# Revit family: PRD_AR_WCSqtngPns_CampusSquatPan_CMPX504
name_source: partatom
category: Plumbing Fixtures
revit_build: Autodesk Revit 2018 (Build: 20190510_1515(x64)
units: mm (PartAtom-declared; Revit-internal decimal feet)

## family parameters
Always vertical = Yes
Cut with Voids When Loaded = Yes
OmniClass Number = 23.45.05.21.11.11
OmniClass Title = Water Operated Water Closets
Part Type = Normal
Room Calculation Point = No
Round Connector Dimension = Use Diameter
Shared = No
Work Plane-Based = No

## types (1)
- CMPX504
    AssetType = Fixed
    BIMObjectName = PRD_AR_WCSquattingPans_CampusSquatPan_CMPX504
    Category = Pr_40_20_93_96, WC squatting pans
    Color = Chrome
    Description = Squat pan made of stainless steel, suitable for DN 20 in-wall flush valves, surface satin finished, material thickness 1 mm, 9 liter flushing capacity, with circular folded edge (22 mm) and circular flushing rim. Vertical connection from behind with screw connection of 28 mm diameter, internal DN 100 waste outlet, fixing material and height adjustment included.
    DurationUnit = year
    Features = stainless steel, 1.00 mm, satin finished, inset floor mounting, 755x185x755 mm (WxHxD)
    Finish = Satin finished
    Form = Squatting, washdown
    GrossWeight = 16.00 kg
    IfcExportAs = IfcSanitaryTerminalType
    IfcExportType = TOILETPAN
    IntegralAccessories = Internal DN 100 waste outlet, fixing material and height adjustment included.
    Manufacturer = KWC Group AG
    ManufacturerName = KWC Group AG
    ManufacturerURL = www.kwc.com
    MaterialsBody = Stainless steel 1.4301
    MaterialsFinishAndColour = Stainless steel, satin finished
    Model = CMPX504
    ModelNumber = 2000102732
    ModelReference = CMPX504
    MountingSupport = Yes
    NBSDescription = WC squatting pans
    NBSReference = 45-35-70/385
    Name = CAMPUS squat pan CMPX504
    NetWeight = 14.50 kg
    NominalDepth = 755 mm  [stored 2.47703 ft]
    NominalHeight = 200 mm  [stored 0.656168 ft]
    NominalLength = 200 mm  [stored 0.656168 ft]
    NominalWidth = 755 mm  [stored 2.47703 ft]
    PanColor = Stainless steel
    PanMaterial = Stainless steel
    PanMounting = Other
    ProductInformation = https://pim.kwc.com
    Shape = Rectangular
    Size = 755 x 200 x 755 mm
    SpilloverLevel = 0 mm  [stored 0 ft]
    SquatPanMaterial = PRD_AR_StainlessSteel_SatinFinished
    ToiletPanType = Squat
    ToiletType = Other
    URL = www.kwc.com
    Uniclass2015Code = Pr_40_20_93_96
    Uniclass2015Title = WC squatting pans
    Uniclass2015Version = Products v1.7
    Version = 1
    WarrantyDurationUnit = year
    WaterSupplyAndOutletOutlet = DN 100, 4inch
    WaterSupplyAndOutletWaterSupply = DN 40, 1 1-2inch

note: [stored X ft] marks values corroborated as IEEE doubles in the binary element streams (Revit-internal decimal feet)

## geometry (parser evidence)
native form markers: Sweep x7
no freeform markers — native parametric forms only
